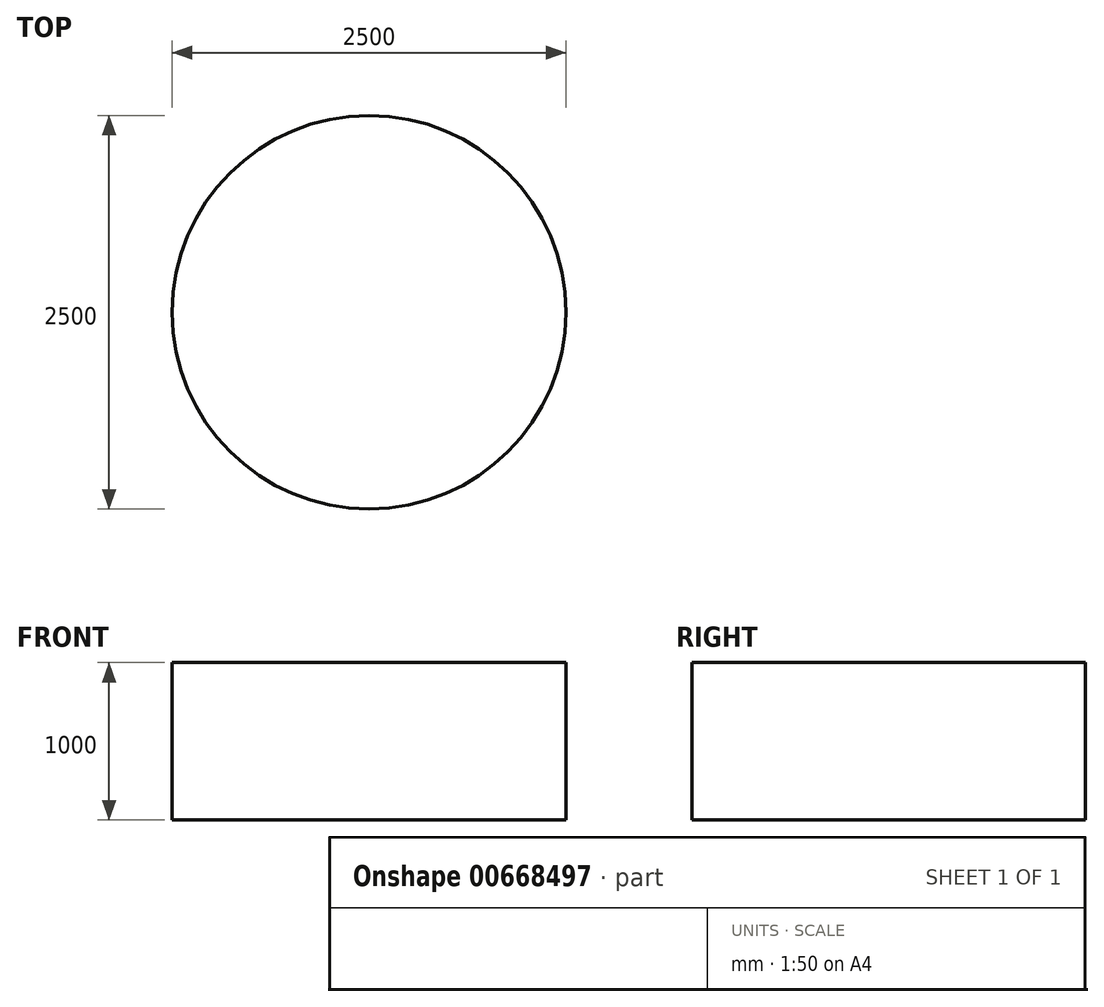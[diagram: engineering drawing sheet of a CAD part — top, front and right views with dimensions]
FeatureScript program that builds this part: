
annotation { "Feature Type Name" : "Feature", "Feature Type Description" : "" }
export const myFeature = defineFeature(function(context is Context, id is Id, definition is map)
    precondition{}
    {
        {
            var Q0;
            Q0=qCreatedBy(makeId("Top.planeOp"),FACE);
            var sketch = newSketch(context, id + "F0", { "sketchPlane" : qUnion([Q0])});
            skCircle(sketch, "E0", {"center": v(0, 0) * mm, "radius": 1250 * mm});
            skSolve(sketch);
        }
        {
            var Q0;
            Q0=makeQuery(id+"F0.imprint","IMPRINT",FACE,{"disambiguationData":[TD([[makeQuery(id+"F0.imprint","IMPRINT",EDGE,{"derivedFrom":sQuery(id+"F0.wireOp",EDGE,"E0")}),1.0]])]});
            extrude(context, id + "F1", {"entities" : qUnion([Q0]), "depth" : 1000 * mm, "offsetDistance" : 25 * mm});
        }
    });
